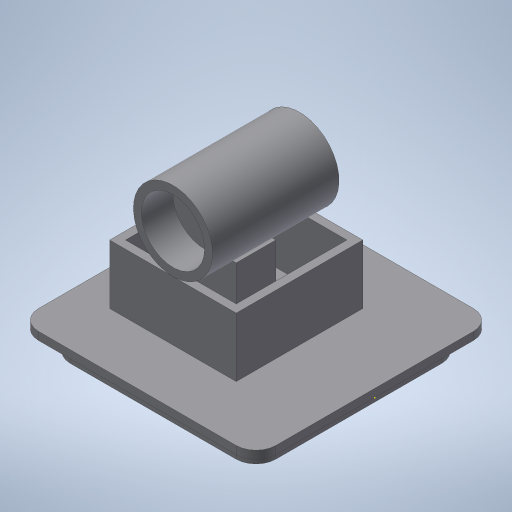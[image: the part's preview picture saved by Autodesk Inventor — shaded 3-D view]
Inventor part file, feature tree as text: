
AUTODESK INVENTOR PART (.ipt)
format: ipt  version: 2023.1 (Build 271208000, 208)  size: 396,288 bytes
history: native  units: mm
features: sketch x15, extrude x13, projected_geometry x11, plane x2, fillet x2
ambient origin geometry x8: Origin, YZ Plane, XZ Plane, XY Plane, X Axis, Y Axis, Z Axis, Center Point
bodies: Solid1 (feature_tree)
feature tree (43):
  extrude  "Extrusion1"  Depth=60.0mm
  extrude  "Extrusion2"  Depth=6.0mm
  sketch  "Sketch10"  dims[d25=-5.0mm d26=5.0mm d27=10.0mm]
  extrude  "Extrusion9"  Depth=5.0mm TaperAngle=0.0deg
  extrude  "Extrusion10"  Depth=32.0mm
  plane  "Work Plane3"
  sketch  "Sketch13"  dims[d34=2.0mm d35=8.0mm d36=0.0mm]
  extrude  "Extrusion11"  Depth=28.0mm
  extrude  "Extrusion12"  Depth=10.0mm
  extrude  "Extrusion13"  Depth=15.0mm TaperAngle=0.0deg
  extrude  "Extrusion14"  Depth=5.0mm
  fillet  "Fillet2"  Radius=10.0mm
  extrude  "Extrusion3"  Depth=32.0mm TaperAngle=0.0deg
  extrude  "Extrusion4"  Depth=8.0mm TaperAngle=0.0deg
  plane  "Work Plane1"
  extrude  "Extrusion5"  Depth=8.0mm TaperAngle=0.0deg
  extrude  "Extrusion6"  Depth=9.0mm
  extrude  "Extrusion7"  Depth=32.0mm
  fillet  "Fillet1"  Radius=32.0mm
  sketch  "Sketch1"  dims[d0=60.0mm d1=60.0mm]
  sketch  "Sketch2"  dims[d2=2.0mm d3=0.0mm d4=6.0mm]
  projected_geometry  "Projected Loop1"
  sketch  "Sketch4"  dims[d5=4.0mm d6=5.0mm d7=0.0mm]
  projected_geometry  "Projected Loop3"
  sketch  "Sketch5"  dims[d15=32.0mm d16=32.0mm]
  projected_geometry  "Projected Loop4"
  sketch  "Sketch6"  dims[d17=28.0mm d18=28.0mm]
  sketch  "Sketch7"  dims[d19=15.0mm d20=0.0mm d21=10.0mm]
  projected_geometry  "Projected Loop5"
  sketch  "Sketch8"  dims[d22=10.0mm d23=15.0mm d24=0.0mm]
  projected_geometry  "Projected Loop6"
  projected_geometry  "Projected Loop8"
  sketch  "Sketch11"  dims[d28=20.0mm d29=32.0mm d30=0.0mm]
  projected_geometry  "Projected Loop9"
  sketch  "Sketch12"  dims[d31=2.0mm d32=8.0mm d33=0.0mm]
  projected_geometry  "Projected Loop10"
  sketch  "Sketch14"  dims[d42=5.0mm d43=9.0mm]
  sketch  "Sketch15"  dims[d44=16.0mm d45=32.0mm d46=32.0mm]
  projected_geometry  "Projected Loop11"
  sketch  "Sketch16"  dims[d47=2.0mm]
  projected_geometry  "Projected Loop12"
  sketch  "Sketch17"  dims[d48=28.0mm d49=9.0mm d50=16.0mm d51=32.0mm d52=32.0mm d53=2.0mm d54=14.0mm d55=28.0mm d56=28.0mm d57=28.0mm d58=28.0mm d59=15.0mm d60=0.0mm d61=10.0mm d62=10.0mm d63=10.0mm d64=10.0mm d65=15.0mm d66=0.0mm d67=-5.0mm d68=5.0mm d69=10.0mm d70=20.0mm d71=32.0mm d72=0.0mm d73=2.0mm d74=8.0mm d75=0.0mm d76=2.0mm d77=8.0mm d78=0.0mm d79=4.5mm d80=7.0mm d81=7.0mm d82=8.0mm d83=0.0mm d84=5.0mm]
  projected_geometry  "Projected Loop13"
